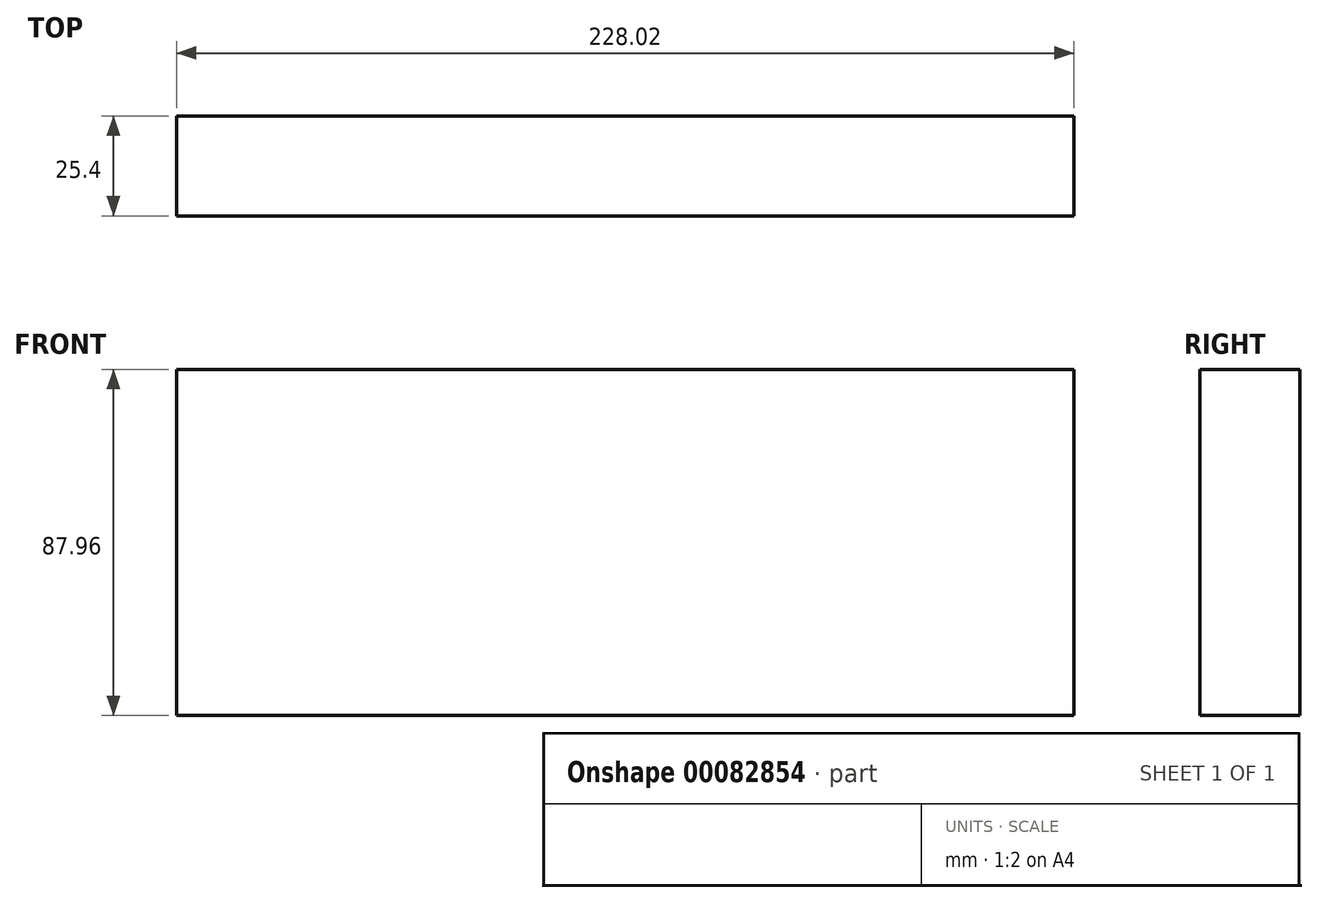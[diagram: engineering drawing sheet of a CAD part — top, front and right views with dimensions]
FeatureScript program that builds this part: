
annotation { "Feature Type Name" : "Feature", "Feature Type Description" : "" }
export const myFeature = defineFeature(function(context is Context, id is Id, definition is map)
    precondition{}
    {
        {
            var Q0;
            Q0=qCreatedBy(makeId("Front.planeOp"),FACE);
            var sketch = newSketch(context, id + "F0", { "sketchPlane" : qUnion([Q0])});
            skLineSegment(sketch, "E0.bottom", {"start": v(-103.06, 57.82) * mm, "end": v(124.96, 57.82) * mm});
            skLineSegment(sketch, "E0.top", {"start": v(-103.06, -30.14) * mm, "end": v(124.96, -30.14) * mm});
            skLineSegment(sketch, "E0.left", {"start": v(-103.06, 57.82) * mm, "end": v(-103.06, -30.14) * mm});
            skLineSegment(sketch, "E0.right", {"start": v(124.96, 57.82) * mm, "end": v(124.96, -30.14) * mm});
            skSolve(sketch);
        }
        {
            var Q0;
            Q0=makeQuery(id+"F0.imprint","IMPRINT",FACE,{"disambiguationData":[TD([[makeQuery(id+"F0.imprint","IMPRINT",EDGE,{"derivedFrom":sQuery(id+"F0.wireOp",EDGE,"E0.bottom")}),-1.0]])]});
            extrude(context, id + "F1", {"entities" : qUnion([Q0]), "depth" : 25.4 * mm});
        }
    });
